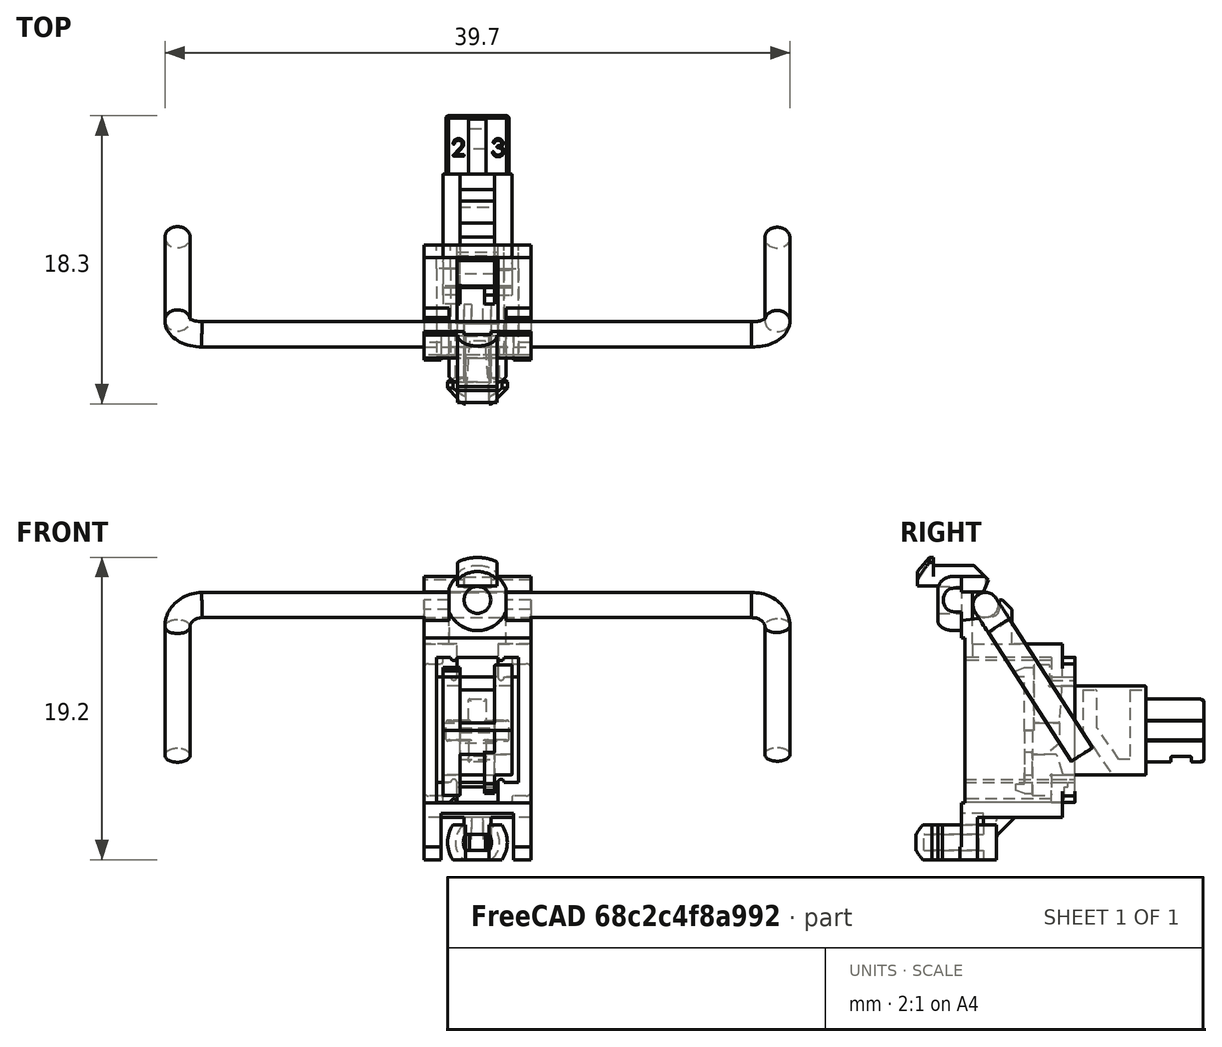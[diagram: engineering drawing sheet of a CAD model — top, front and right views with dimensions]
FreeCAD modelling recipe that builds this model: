
FCSTD DOCUMENT  (FreeCAD 0.18R16158 (Git))
Label: Stabilizer_Cherry_MX_3u
License: CreativeCommons Attribution-ShareAlike
LicenseURL: http://creativecommons.org/licenses/by-sa/4.0/
objects: Part::Feature×4, App::Part×3, PartDesign::Plane×2, Sketcher::SketchObject×2, PartDesign::AdditivePipe×1, PartDesign::Body×1
note: 11 computed .brp shape members not serialized (recipe doc carries the construction recipe); baked Part::Feature solids carry a one-line shape summary decoded from their .brp

FEATURE [Part::Feature] Part__Feature  label="Stabilizer_Base"
  shape: bbox 6.802 x 10.1 x 19.67 mm, 163 faces (baked)
FEATURE [Part::Feature] Part__Feature001  label="Stabilizer_Key"
  Placement = pos=(0,8.1,0) rot=(0,0,1;0rad)
  shape: bbox 4.6 x 11.96 x 8.302 mm, 299 faces (baked)
FEATURE [App::Part] Part  label="Stabilizer_End_1"
  Group = -> [Part__Feature001,Part__Feature]
  Origin = -> Origin001
  Placement = pos=(-19.05,0,0) rot=(0,0,1;0rad)
FEATURE [PartDesign::Plane] DatumPlane
  Length = 49.7646
  MapMode = 13
  Placement = pos=(23.0333,0.289849,4.3056) rot=(1,0,0;2.14498rad)
  ResizeMode = 0
  Width = 34.5428
FEATURE [PartDesign::Plane] DatumPlane001
  Length = 34.2816
  MapMode = 11
  Placement = pos=(8e-15,4.09188,-1.57187) rot=(0.272451,-0.272451,0.92279;1.65106rad)
  ResizeMode = 0
  Width = 46.3124
FEATURE [Sketcher::SketchObject] Sketch
  MapMode = 5
  Placement = pos=(8e-15,4.09188,-1.57187) rot=(0.272451,-0.272451,0.92279;1.65106rad)
  Support = -> [DatumPlane001]
  sketch-geometry (5):
    g0: Circle CenterX=0 CenterY=19.05 CenterZ=0 NormalX=0 NormalY=0 NormalZ=1 AngleXU=0 Radius=0.8
    g1: Circle [constr] CenterX=0 CenterY=-19.05 CenterZ=0 NormalX=0 NormalY=0 NormalZ=1 AngleXU=0 Radius=0.8
    g2: LineSegment [constr] StartX=0 StartY=19.05 StartZ=0 EndX=0 EndY=0 EndZ=0
    g3: LineSegment [constr] StartX=0 StartY=0 StartZ=0 EndX=0 EndY=-19.05 EndZ=0
    g4: GeomPoint X=0 Y=-19.05 Z=0
  constraints (11):
    c: Diameter(g0) = 1.6
    c: PointOnObject(g0,g-2)
    c: PointOnObject(g1,g-2)
    c: Coincident(g2,g0)
    c: Coincident(g2,g-1)
    c: Coincident(g3,g-1)
    c: Coincident(g3,g1)
    c: Equal(g3,g2)
    c: Distance(g2) = 19.05
    c: Equal(g1,g0)
    c: Coincident(g4,g1)
FEATURE [Sketcher::SketchObject] Sketch001
  ExternalGeometry = -> [Sketch]
  MapMode = 5
  Placement = pos=(23.0333,0.289849,4.3056) rot=(1,0,0;2.14498rad)
  Support = -> [DatumPlane]
  sketch-geometry (5):
    g0: LineSegment StartX=-41.2842 StartY=-6.96225 StartZ=0 EndX=-41.2842 EndY=2.76775 EndZ=0
    g1: LineSegment StartX=-40.4842 StartY=3.56775 StartZ=0 EndX=-5.58422 EndY=3.56775 EndZ=0
    g2: LineSegment StartX=-4.78422 StartY=2.76775 StartZ=0 EndX=-4.78422 EndY=-6.96225 EndZ=0
    g3: ArcOfCircle CenterX=-40.4842 CenterY=2.76775 CenterZ=0 NormalX=0 NormalY=0 NormalZ=1 AngleXU=0 Radius=0.8 StartAngle=1.5708 EndAngle=3.14159
    g4: ArcOfCircle CenterX=-5.58422 CenterY=2.76775 CenterZ=0 NormalX=0 NormalY=0 NormalZ=1 AngleXU=0 Radius=0.8 StartAngle=-1.9549e-12 EndAngle=1.5708
FEATURE [PartDesign::AdditivePipe] AdditivePipe
  AuxilleryCurvelinear = true
  AuxillerySpineTangent = false
  Binormal = (0,0,0)
  Mode = 0
  Placement = pos=(8e-15,4.09188,-1.57187) rot=(0.272451,-0.272451,0.92279;1.65106rad)
  Profile = -> Sketch
  Spine = -> Sketch001
  SpineTangent = false
  Transformation = 0
  Transition = 0
FEATURE [PartDesign::Body] Body  label="Bar"
  Group = -> [DatumPlane,DatumPlane001,Sketch,Sketch001,AdditivePipe]
  Origin = -> Origin002
  Tip = -> AdditivePipe
FEATURE [Part::Feature] Part__Feature002  label="Stabilizer_Key_"
  Placement = pos=(0,8.1,0) rot=(0,0,1;0rad)
  shape: bbox 4.6 x 11.96 x 8.302 mm, 299 faces (baked)
FEATURE [Part::Feature] Part__Feature003  label="Stabilizer_Base_"
  shape: bbox 6.802 x 10.1 x 19.67 mm, 163 faces (baked)
FEATURE [App::Part] Part001  label="Stabilizer_End_2"
  Group = -> [Part__Feature002,Part__Feature003]
  Origin = -> Origin003
  Placement = pos=(19.05,0,0) rot=(0,0,1;0rad)
FEATURE [App::Part] Stabilizer___open  label="Stabilizer_Cherry_MX_3u"
  Group = -> [Body,Part001,Part]
  Origin = -> Origin
  Placement = pos=(0,8e-16,3.65) rot=(1,0,0;1.5708rad)
